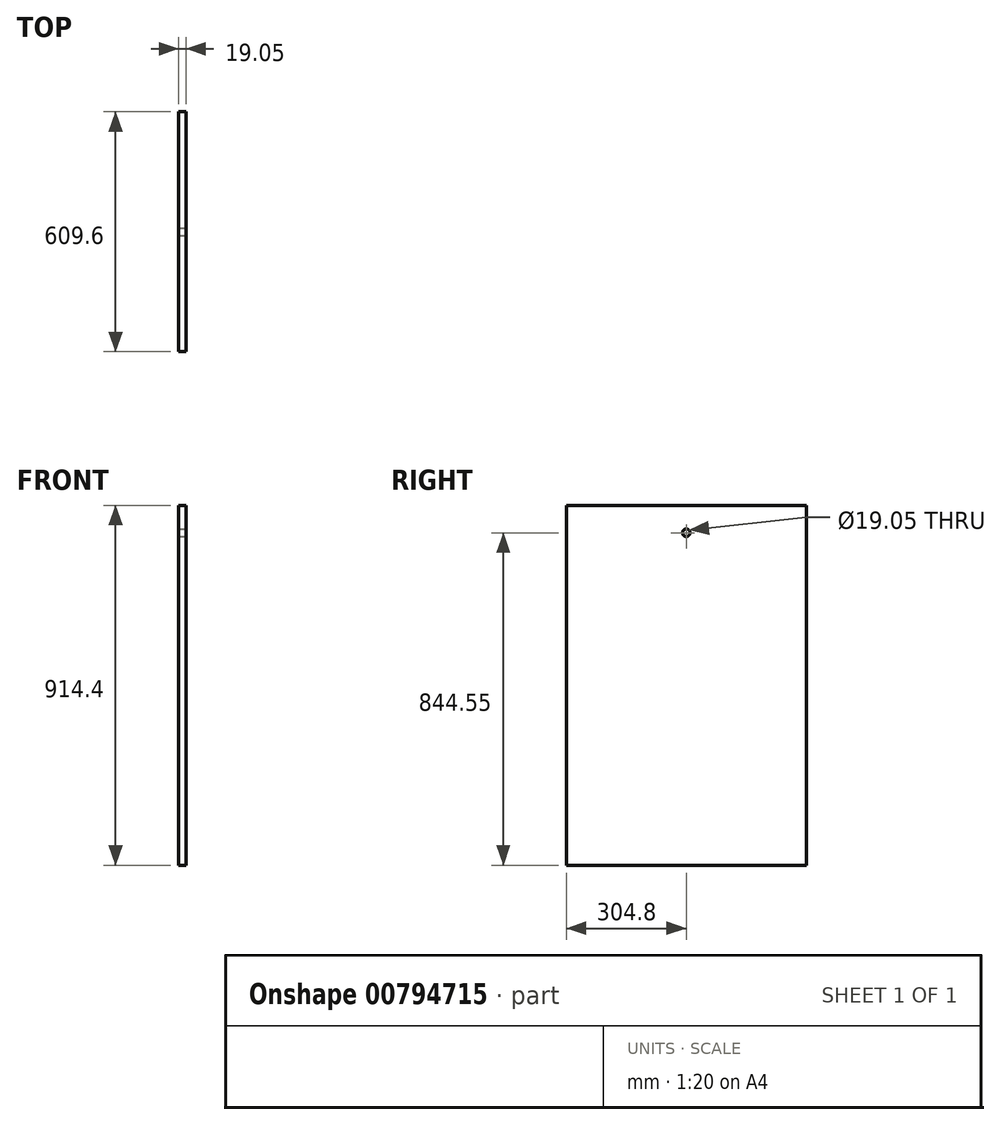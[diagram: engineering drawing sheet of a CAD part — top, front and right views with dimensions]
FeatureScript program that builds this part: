
annotation { "Feature Type Name" : "Feature", "Feature Type Description" : "" }
export const myFeature = defineFeature(function(context is Context, id is Id, definition is map)
    precondition{}
    {
        {
            var Q0;
            Q0=qCreatedBy(makeId("Right.planeOp"),FACE);
            var sketch = newSketch(context, id + "F0", { "sketchPlane" : qUnion([Q0])});
            skLineSegment(sketch, "E0.bottom", {"start": v(304.8, -457.2) * mm, "end": v(-304.8, -457.2) * mm});
            skLineSegment(sketch, "E0.top", {"start": v(304.8, 457.2) * mm, "end": v(-304.8, 457.2) * mm});
            skLineSegment(sketch, "E0.left", {"start": v(304.8, -457.2) * mm, "end": v(304.8, 457.2) * mm});
            skLineSegment(sketch, "E0.right", {"start": v(-304.8, -457.2) * mm, "end": v(-304.8, 457.2) * mm});
            skPoint(sketch, "E0.middle", {"position": v(0, 0) * mm});
            skSolve(sketch);
        }
        {
            var Q0;
            Q0 = qSketchRegion(id + "F0", true);
            extrude(context, id + "F1", {"entities" : qUnion([Q0]), "depth" : 19.05 * mm, "offsetDistance" : 25.4 * mm});
        }
        {
            var Q0;
            Q0=makeQuery(id+"F1.opExtrude","CAP_FACE",FACE,{"disambiguationData":[OSD([sQuery(id+"F0.wireOp",EDGE,"E0.bottom"),sQuery(id+"F0.wireOp",EDGE,"E0.top"),sQuery(id+"F0.wireOp",EDGE,"E0.left"),sQuery(id+"F0.wireOp",EDGE,"E0.right")])],"isStart":false});
            var sketch = newSketch(context, id + "F2", { "sketchPlane" : qUnion([Q0])});
            skLineSegment(sketch, "E1", {"start": v(0, 457.2) * mm, "end": v(0, 387.35) * mm, "construction": true});
            skCircle(sketch, "E2", {"center": v(0, 387.35) * mm, "radius": 9.53 * mm});
            skSolve(sketch);
        }
        {
            var Q0;
            Q0 = qSketchRegion(id + "F2", true);
            extrude(context, id + "F3", {"entities" : qUnion([Q0]), "operationType" : NewBodyOperationType.REMOVE, "oppositeDirection" : true, "depth" : 25.4 * mm, "offsetDistance" : 25.4 * mm});
        }
    });
